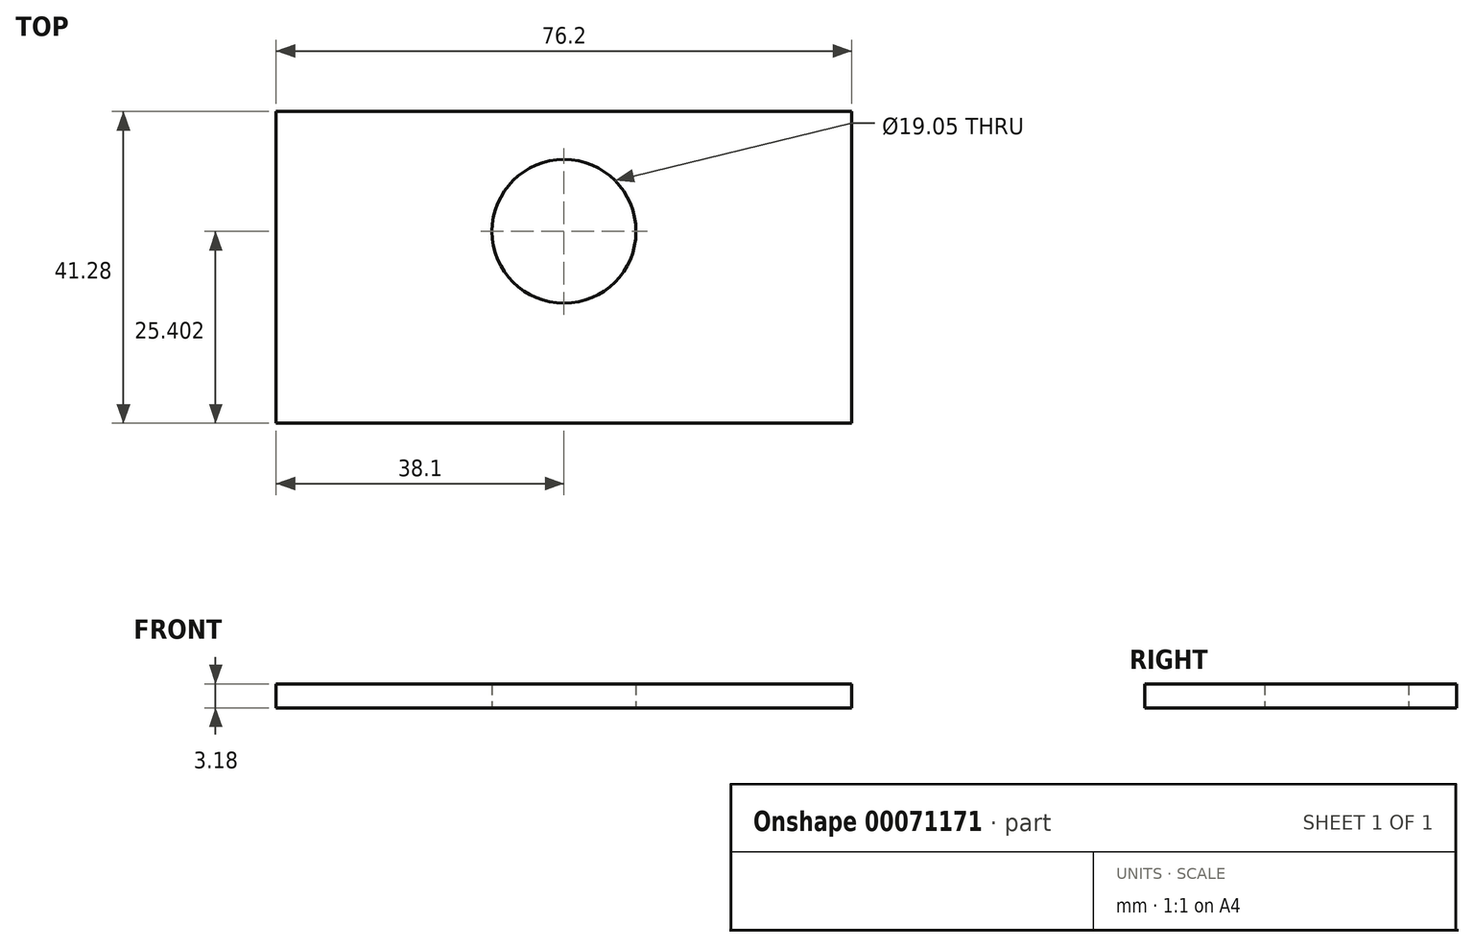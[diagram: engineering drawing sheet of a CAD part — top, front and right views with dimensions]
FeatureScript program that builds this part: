
annotation { "Feature Type Name" : "Feature", "Feature Type Description" : "" }
export const myFeature = defineFeature(function(context is Context, id is Id, definition is map)
    precondition{}
    {
        {
            var Q0;
            Q0=qCreatedBy(makeId("Top.planeOp"),FACE);
            var sketch = newSketch(context, id + "F0", { "sketchPlane" : qUnion([Q0])});
            skLineSegment(sketch, "E0.rect.bottom", {"start": v(38.1, 20.64) * mm, "end": v(-38.1, 20.64) * mm});
            skLineSegment(sketch, "E0.rect.top", {"start": v(38.1, -20.64) * mm, "end": v(-38.1, -20.64) * mm});
            skLineSegment(sketch, "E0.rect.left", {"start": v(38.1, 20.64) * mm, "end": v(38.1, -20.64) * mm});
            skLineSegment(sketch, "E0.rect.right", {"start": v(-38.1, 20.64) * mm, "end": v(-38.1, -20.64) * mm});
            skPoint(sketch, "E0.rect.middle", {"position": v(0, 0) * mm});
            skCircle(sketch, "E1", {"center": v(0, 4.76) * mm, "radius": 9.53 * mm});
            skSolve(sketch);
        }
        {
            var Q0;
            Q0=makeQuery(id+"F0.imprint","IMPRINT",FACE,{"disambiguationData":[TD([[makeQuery(id+"F0.imprint","IMPRINT",EDGE,{"derivedFrom":sQuery(id+"F0.wireOp",EDGE,"E0.rect.bottom")}),1.0]])]});
            extrude(context, id + "F1", {"entities" : qUnion([Q0]), "depth" : 3.17 * mm});
        }
    });
